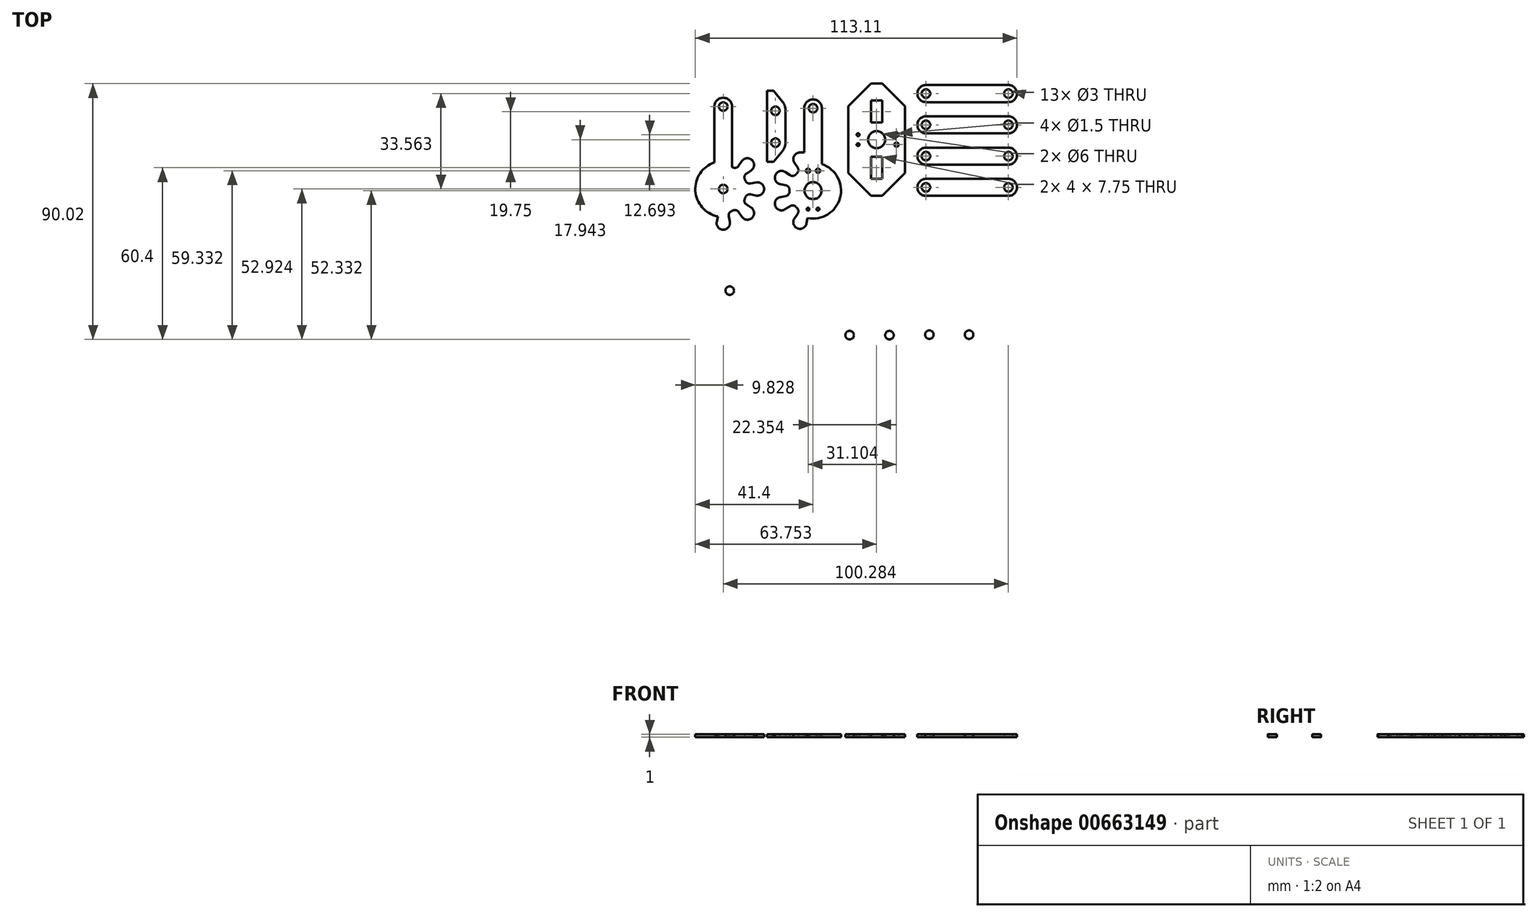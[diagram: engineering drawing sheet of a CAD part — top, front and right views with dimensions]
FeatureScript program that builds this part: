
annotation { "Feature Type Name" : "Feature", "Feature Type Description" : "" }
export const myFeature = defineFeature(function(context is Context, id is Id, definition is map)
    precondition{}
    {
        {
            var Q0;
            Q0=qCreatedBy(makeId("Top.planeOp"),FACE);
            var sketch = newSketch(context, id + "F0", { "sketchPlane" : qUnion([Q0])});
            skCircle(sketch, "E0", {"center": v(-44.1, -27.1) * mm, "radius": 1.5 * mm});
            skLineSegment(sketch, "E1", {"start": v(-8.4, -41.1) * mm, "end": v(-8.4, -22.47) * mm});
            skLineSegment(sketch, "E2", {"start": v(-26.87, -6.6) * mm, "end": v(-38.44, -6.6) * mm});
            skLineSegment(sketch, "E3", {"start": v(-56.9, -22.47) * mm, "end": v(-56.9, -41.1) * mm});
            skCircle(sketch, "E4", {"center": v(-38.1, -10.13) * mm, "radius": 1.5 * mm});
            skCircle(sketch, "E5", {"center": v(-26.9, -10.13) * mm, "radius": 1.5 * mm});
            skLineSegment(sketch, "E6", {"start": v(-14.3, -20.65) * mm, "end": v(-37, -20.65) * mm, "construction": true});
            skLineSegment(sketch, "E7", {"start": v(-37, -33.55) * mm, "end": v(-14.3, -33.55) * mm, "construction": true});
            skLineSegment(sketch, "E8", {"start": v(-14.3, -20.65) * mm, "end": v(-14.3, -33.55) * mm, "construction": true});
            skLineSegment(sketch, "E9", {"start": v(-37, -20.65) * mm, "end": v(-37, -33.55) * mm, "construction": true});
            skLineSegment(sketch, "E10", {"start": v(-9.72, -19.29) * mm, "end": v(-24.02, -7.62) * mm});
            skLineSegment(sketch, "E11", {"start": v(-41.28, -7.62) * mm, "end": v(-55.58, -19.29) * mm});
            skArc(sketch, "E12", {"start": v(-8.4, -22.47) * mm, "mid": v(-8.74, -20.75) * mm, "end": v(-9.72, -19.29) * mm});
            skArc(sketch, "E13", {"start": v(-55.58, -19.29) * mm, "mid": v(-56.56, -20.75) * mm, "end": v(-56.9, -22.47) * mm});
            skArc(sketch, "E14", {"start": v(-12.9, -45.6) * mm, "mid": v(-9.72, -44.29) * mm, "end": v(-8.4, -41.1) * mm});
            skArc(sketch, "E15", {"start": v(-56.9, -41.1) * mm, "mid": v(-55.58, -44.29) * mm, "end": v(-52.4, -45.6) * mm});
            skLineSegment(sketch, "E16", {"start": v(-52.4, -45.6) * mm, "end": v(-52.4, -41.6) * mm});
            skLineSegment(sketch, "E17", {"start": v(-52.4, -41.6) * mm, "end": v(-46.4, -41.6) * mm});
            skLineSegment(sketch, "E18", {"start": v(-46.4, -41.6) * mm, "end": v(-46.4, -45.6) * mm});
            skLineSegment(sketch, "E19", {"start": v(-12.9, -45.6) * mm, "end": v(-12.9, -41.6) * mm});
            skLineSegment(sketch, "E20", {"start": v(-12.9, -41.6) * mm, "end": v(-18.9, -41.6) * mm});
            skLineSegment(sketch, "E21", {"start": v(-18.9, -41.6) * mm, "end": v(-18.9, -45.6) * mm});
            skLineSegment(sketch, "E22", {"start": v(-38.65, -41.6) * mm, "end": v(-26.65, -41.6) * mm});
            skLineSegment(sketch, "E23", {"start": v(-26.65, -41.6) * mm, "end": v(-26.65, -45.6) * mm});
            skLineSegment(sketch, "E24", {"start": v(-38.65, -41.6) * mm, "end": v(-38.65, -45.6) * mm});
            skArc(sketch, "E25", {"start": v(-24.02, -7.62) * mm, "mid": v(-25.36, -6.86) * mm, "end": v(-26.87, -6.6) * mm});
            skArc(sketch, "E26", {"start": v(-38.44, -6.6) * mm, "mid": v(-39.95, -6.86) * mm, "end": v(-41.28, -7.62) * mm});
            skLineSegment(sketch, "E27", {"start": v(-46.4, -45.6) * mm, "end": v(-38.65, -45.6) * mm});
            skLineSegment(sketch, "E28", {"start": v(-26.65, -45.6) * mm, "end": v(-18.9, -45.6) * mm});
            skCircle(sketch, "E29", {"center": v(-39.9, -27.1) * mm, "radius": 0.9 * mm});
            skCircle(sketch, "E30", {"center": v(-11.4, -27.1) * mm, "radius": 0.9 * mm});
            skCircle(sketch, "E31", {"center": v(-11, -8.76) * mm, "radius": 3 * mm});
            skCircle(sketch, "E32", {"center": v(-11, -8.76) * mm, "radius": 1.5 * mm});
            skCircle(sketch, "E33", {"center": v(12.07, -42.76) * mm, "radius": 1.5 * mm});
            skCircle(sketch, "E34", {"center": v(18.07, -25.8) * mm, "radius": 1.5 * mm});
            skLineSegment(sketch, "E35", {"start": v(23.57, -22.8) * mm, "end": v(23.57, 2.2) * mm});
            skLineSegment(sketch, "E36", {"start": v(23.57, 2.2) * mm, "end": v(17.07, 2.2) * mm});
            skLineSegment(sketch, "E37", {"start": v(17.07, 2.2) * mm, "end": v(17.07, -22.8) * mm});
            skLineSegment(sketch, "E38", {"start": v(17.07, -22.8) * mm, "end": v(15.57, -22.8) * mm});
            skLineSegment(sketch, "E39", {"start": v(9.2, -41.89) * mm, "end": v(15.57, -22.8) * mm});
            skLineSegment(sketch, "E40", {"start": v(14.87, -43.83) * mm, "end": v(23.57, -22.8) * mm});
            skArc(sketch, "E41", {"start": v(9.2, -41.89) * mm, "mid": v(11.1, -45.6) * mm, "end": v(14.87, -43.83) * mm});
            skLineSegment(sketch, "E42", {"start": v(24.9, 45.23) * mm, "end": v(53.9, 45.23) * mm});
            skLineSegment(sketch, "E43", {"start": v(53.9, 39.23) * mm, "end": v(24.9, 39.23) * mm});
            skArc(sketch, "E44", {"start": v(24.9, 45.23) * mm, "mid": v(21.9, 42.23) * mm, "end": v(24.9, 39.23) * mm});
            skArc(sketch, "E45", {"start": v(53.9, 39.23) * mm, "mid": v(56.9, 42.23) * mm, "end": v(53.9, 45.23) * mm});
            skCircle(sketch, "E46", {"center": v(24.9, 42.23) * mm, "radius": 1.5 * mm});
            skCircle(sketch, "E47", {"center": v(53.9, 42.23) * mm, "radius": 1.5 * mm});
            skLineSegment(sketch, "E48", {"start": v(17.54, 37.76) * mm, "end": v(17.54, 14.26) * mm});
            skLineSegment(sketch, "E49", {"start": v(9.54, 6.26) * mm, "end": v(17.54, 14.26) * mm});
            skLineSegment(sketch, "E50", {"start": v(9.54, 6.26) * mm, "end": v(5.54, 6.26) * mm});
            skLineSegment(sketch, "E51", {"start": v(-2.46, 14.26) * mm, "end": v(5.54, 6.26) * mm});
            skLineSegment(sketch, "E52", {"start": v(-2.46, 14.26) * mm, "end": v(-2.46, 37.76) * mm});
            skLineSegment(sketch, "E53", {"start": v(5.54, 45.76) * mm, "end": v(9.54, 45.76) * mm});
            skLineSegment(sketch, "E54", {"start": v(-2.46, 37.76) * mm, "end": v(5.54, 45.76) * mm});
            skLineSegment(sketch, "E55", {"start": v(17.54, 37.76) * mm, "end": v(9.54, 45.76) * mm});
            skLineSegment(sketch, "E56", {"start": v(5.54, 39.76) * mm, "end": v(9.54, 39.76) * mm});
            skLineSegment(sketch, "E57", {"start": v(9.54, 39.76) * mm, "end": v(9.54, 32.01) * mm});
            skLineSegment(sketch, "E58", {"start": v(9.54, 32.01) * mm, "end": v(5.54, 32.01) * mm});
            skLineSegment(sketch, "E59", {"start": v(5.54, 32.01) * mm, "end": v(5.54, 39.76) * mm});
            skLineSegment(sketch, "E60", {"start": v(5.54, 20.01) * mm, "end": v(9.54, 20.01) * mm});
            skLineSegment(sketch, "E61", {"start": v(9.54, 20.01) * mm, "end": v(9.54, 12.26) * mm});
            skLineSegment(sketch, "E62", {"start": v(9.54, 12.26) * mm, "end": v(5.54, 12.26) * mm});
            skLineSegment(sketch, "E63", {"start": v(5.54, 12.26) * mm, "end": v(5.54, 20.01) * mm});
            skCircle(sketch, "E64", {"center": v(7.54, 26.01) * mm, "radius": 3 * mm});
            skCircle(sketch, "E65", {"center": v(14.54, 27.76) * mm, "radius": 0.75 * mm});
            skCircle(sketch, "E66", {"center": v(14.54, 24.26) * mm, "radius": 0.75 * mm});
            skCircle(sketch, "E67", {"center": v(1.04, 27.76) * mm, "radius": 0.5 * mm});
            skCircle(sketch, "E68", {"center": v(1.04, 24.26) * mm, "radius": 0.5 * mm});
            skLineSegment(sketch, "E69", {"start": v(-40.97, 0.55) * mm, "end": v(-39.86, -1.12) * mm});
            skArc(sketch, "E70", {"start": v(-40.97, 0.55) * mm, "mid": v(-41.85, 1.19) * mm, "end": v(-42.93, 1.1) * mm});
            skArc(sketch, "E71", {"start": v(-43.48, 0.88) * mm, "mid": v(-43.2, 0.99) * mm, "end": v(-42.93, 1.1) * mm});
            skArc(sketch, "E72", {"start": v(-43.48, 0.88) * mm, "mid": v(-44.3, 0.17) * mm, "end": v(-44.47, -0.9) * mm});
            skLineSegment(sketch, "E73", {"start": v(-44.07, -2.86) * mm, "end": v(-44.47, -0.9) * mm});
            skArc(sketch, "E74", {"start": v(-44.04, -3.08) * mm, "mid": v(-44.05, -2.97) * mm, "end": v(-44.07, -2.86) * mm});
            skArc(sketch, "E75", {"start": v(-48.69, -2.86) * mm, "mid": v(-48.7, -2.97) * mm, "end": v(-48.72, -3.08) * mm});
            skLineSegment(sketch, "E76", {"start": v(-48.31, -0.98) * mm, "end": v(-48.69, -2.86) * mm});
            skArc(sketch, "E77", {"start": v(-42.93, 16.22) * mm, "mid": v(-43.1, 16.3) * mm, "end": v(-43.28, 16.37) * mm});
            skArc(sketch, "E78", {"start": v(-42.93, 16.22) * mm, "mid": v(-41.85, 16.14) * mm, "end": v(-40.97, 16.78) * mm});
            skLineSegment(sketch, "E79", {"start": v(-39.86, 18.45) * mm, "end": v(-40.97, 16.78) * mm});
            skArc(sketch, "E80", {"start": v(-39.73, 18.62) * mm, "mid": v(-39.8, 18.54) * mm, "end": v(-39.86, 18.45) * mm});
            skArc(sketch, "E81", {"start": v(-36.6, 15.18) * mm, "mid": v(-36.5, 15.25) * mm, "end": v(-36.42, 15.31) * mm});
            skLineSegment(sketch, "E82", {"start": v(-38.26, 14.07) * mm, "end": v(-36.6, 15.18) * mm});
            skArc(sketch, "E83", {"start": v(-38.26, 14.07) * mm, "mid": v(-38.9, 13.2) * mm, "end": v(-38.82, 12.12) * mm});
            skArc(sketch, "E84", {"start": v(-38.6, 11.57) * mm, "mid": v(-38.7, 11.84) * mm, "end": v(-38.82, 12.12) * mm});
            skArc(sketch, "E85", {"start": v(-38.6, 11.57) * mm, "mid": v(-37.89, 10.75) * mm, "end": v(-36.82, 10.58) * mm});
            skLineSegment(sketch, "E86", {"start": v(-34.6, 11) * mm, "end": v(-36.82, 10.58) * mm});
            skLineSegment(sketch, "E87", {"start": v(-36.82, 6.75) * mm, "end": v(-34.6, 6.32) * mm});
            skArc(sketch, "E88", {"start": v(-36.82, 6.75) * mm, "mid": v(-37.89, 6.58) * mm, "end": v(-38.6, 5.76) * mm});
            skArc(sketch, "E89", {"start": v(-38.82, 5.21) * mm, "mid": v(-38.7, 5.48) * mm, "end": v(-38.6, 5.76) * mm});
            skArc(sketch, "E90", {"start": v(-38.82, 5.21) * mm, "mid": v(-38.9, 4.13) * mm, "end": v(-38.26, 3.26) * mm});
            skLineSegment(sketch, "E91", {"start": v(-36.6, 2.15) * mm, "end": v(-38.26, 3.26) * mm});
            skArc(sketch, "E92", {"start": v(-36.42, 2.02) * mm, "mid": v(-36.5, 2.08) * mm, "end": v(-36.6, 2.15) * mm});
            skArc(sketch, "E93", {"start": v(-39.86, -1.12) * mm, "mid": v(-39.8, -1.2) * mm, "end": v(-39.73, -1.3) * mm});
            skArc(sketch, "E94", {"start": v(-48.73, -3.1) * mm, "mid": v(-46.38, -5.68) * mm, "end": v(-44.04, -3.1) * mm});
            skArc(sketch, "E95", {"start": v(-34.6, 6.32) * mm, "mid": v(-32.04, 8.66) * mm, "end": v(-34.6, 11) * mm});
            skArc(sketch, "E96", {"start": v(-36.4, 15.33) * mm, "mid": v(-36.24, 18.8) * mm, "end": v(-39.71, 18.65) * mm});
            skArc(sketch, "E97", {"start": v(-39.71, -1.32) * mm, "mid": v(-36.24, -1.48) * mm, "end": v(-36.4, 2) * mm});
            skArc(sketch, "E98", {"start": v(-36.42, 15.31) * mm, "mid": v(-36.41, 15.32) * mm, "end": v(-36.4, 15.33) * mm});
            skArc(sketch, "E99", {"start": v(-39.71, 18.65) * mm, "mid": v(-39.72, 18.63) * mm, "end": v(-39.73, 18.62) * mm});
            skArc(sketch, "E100", {"start": v(-48.72, -3.08) * mm, "mid": v(-48.72, -3.1) * mm, "end": v(-48.73, -3.1) * mm});
            skArc(sketch, "E101", {"start": v(-44.04, -3.1) * mm, "mid": v(-44.04, -3.1) * mm, "end": v(-44.04, -3.08) * mm});
            skArc(sketch, "E102", {"start": v(-39.73, -1.3) * mm, "mid": v(-39.72, -1.3) * mm, "end": v(-39.71, -1.32) * mm});
            skArc(sketch, "E103", {"start": v(-36.4, 2) * mm, "mid": v(-36.41, 2) * mm, "end": v(-36.42, 2.02) * mm});
            skLineSegment(sketch, "E104", {"start": v(-43.28, 37.66) * mm, "end": v(-43.28, 16.37) * mm});
            skLineSegment(sketch, "E105", {"start": v(-49.49, 37.66) * mm, "end": v(-49.49, 18) * mm});
            skArc(sketch, "E106", {"start": v(-49.49, 18) * mm, "mid": v(-56.2, 8.06) * mm, "end": v(-48.31, -0.98) * mm});
            skCircle(sketch, "E107", {"center": v(-46.38, 8.66) * mm, "radius": 1.5 * mm});
            skCircle(sketch, "E108", {"center": v(-46.38, 37.66) * mm, "radius": 1.5 * mm});
            skArc(sketch, "E109", {"start": v(-43.28, 37.66) * mm, "mid": v(-46.38, 40.77) * mm, "end": v(-49.49, 37.66) * mm});
            skLineSegment(sketch, "E110", {"start": v(-24.51, 24.93) * mm, "end": v(-24.51, 36.5) * mm});
            skCircle(sketch, "E111", {"center": v(-28.04, 36.16) * mm, "radius": 1.5 * mm});
            skCircle(sketch, "E112", {"center": v(-28.04, 24.96) * mm, "radius": 1.5 * mm});
            skLineSegment(sketch, "E113", {"start": v(-28.69, 18.2) * mm, "end": v(-25.53, 22.08) * mm});
            skLineSegment(sketch, "E114", {"start": v(-25.53, 39.34) * mm, "end": v(-28.69, 43.2) * mm});
            skArc(sketch, "E115", {"start": v(-25.53, 22.08) * mm, "mid": v(-24.77, 23.42) * mm, "end": v(-24.51, 24.93) * mm});
            skArc(sketch, "E116", {"start": v(-24.51, 36.5) * mm, "mid": v(-24.77, 38) * mm, "end": v(-25.53, 39.34) * mm});
            skLineSegment(sketch, "E117", {"start": v(-31.01, 43.2) * mm, "end": v(-31.01, 18.2) * mm});
            skLineSegment(sketch, "E118", {"start": v(-31.01, 18.2) * mm, "end": v(-28.69, 18.2) * mm});
            skLineSegment(sketch, "E119", {"start": v(-31.01, 43.2) * mm, "end": v(-28.69, 43.2) * mm});
            skLineSegment(sketch, "E120", {"start": v(-11.7, 37.07) * mm, "end": v(-11.7, 17.4) * mm});
            skLineSegment(sketch, "E121", {"start": v(-17.92, 37.07) * mm, "end": v(-17.92, 21.5) * mm});
            skLineSegment(sketch, "E122", {"start": v(-17.09, -3.46) * mm, "end": v(-16.72, -1.57) * mm});
            skArc(sketch, "E123", {"start": v(-17.14, -3.67) * mm, "mid": v(-17.11, -3.57) * mm, "end": v(-17.09, -3.46) * mm});
            skArc(sketch, "E124", {"start": v(-21.35, -1.7) * mm, "mid": v(-21.41, -1.79) * mm, "end": v(-21.47, -1.88) * mm});
            skLineSegment(sketch, "E125", {"start": v(-20.24, -0.03) * mm, "end": v(-21.35, -1.7) * mm});
            skArc(sketch, "E126", {"start": v(-20.24, -0.03) * mm, "mid": v(-19.98, 1.02) * mm, "end": v(-20.47, 2) * mm});
            skArc(sketch, "E127", {"start": v(-20.9, 2.4) * mm, "mid": v(-20.69, 2.2) * mm, "end": v(-20.47, 2) * mm});
            skArc(sketch, "E128", {"start": v(-20.9, 2.4) * mm, "mid": v(-21.86, 2.9) * mm, "end": v(-22.91, 2.64) * mm});
            skLineSegment(sketch, "E129", {"start": v(-24.58, 1.53) * mm, "end": v(-22.91, 2.64) * mm});
            skArc(sketch, "E130", {"start": v(-24.76, 1.42) * mm, "mid": v(-24.67, 1.47) * mm, "end": v(-24.58, 1.53) * mm});
            skArc(sketch, "E131", {"start": v(-26.34, 5.8) * mm, "mid": v(-26.45, 5.77) * mm, "end": v(-26.55, 5.74) * mm});
            skLineSegment(sketch, "E132", {"start": v(-24.38, 6.18) * mm, "end": v(-26.34, 5.8) * mm});
            skArc(sketch, "E133", {"start": v(-24.38, 6.18) * mm, "mid": v(-23.45, 6.75) * mm, "end": v(-23.12, 7.78) * mm});
            skArc(sketch, "E134", {"start": v(-23.12, 8.37) * mm, "mid": v(-23.12, 8.07) * mm, "end": v(-23.12, 7.78) * mm});
            skArc(sketch, "E135", {"start": v(-23.12, 8.37) * mm, "mid": v(-23.45, 9.4) * mm, "end": v(-24.38, 9.96) * mm});
            skLineSegment(sketch, "E136", {"start": v(-26.34, 10.35) * mm, "end": v(-24.38, 9.96) * mm});
            skArc(sketch, "E137", {"start": v(-26.55, 10.4) * mm, "mid": v(-26.45, 10.37) * mm, "end": v(-26.34, 10.35) * mm});
            skArc(sketch, "E138", {"start": v(-24.58, 14.62) * mm, "mid": v(-24.67, 14.67) * mm, "end": v(-24.76, 14.73) * mm});
            skLineSegment(sketch, "E139", {"start": v(-22.91, 13.5) * mm, "end": v(-24.58, 14.62) * mm});
            skArc(sketch, "E140", {"start": v(-22.91, 13.5) * mm, "mid": v(-21.86, 13.25) * mm, "end": v(-20.9, 13.74) * mm});
            skArc(sketch, "E141", {"start": v(-20.47, 14.15) * mm, "mid": v(-20.69, 13.95) * mm, "end": v(-20.9, 13.74) * mm});
            skArc(sketch, "E142", {"start": v(-20.47, 14.15) * mm, "mid": v(-19.98, 15.12) * mm, "end": v(-20.24, 16.18) * mm});
            skLineSegment(sketch, "E143", {"start": v(-21.35, 17.84) * mm, "end": v(-20.24, 16.18) * mm});
            skArc(sketch, "E144", {"start": v(-21.47, 18.02) * mm, "mid": v(-21.41, 17.93) * mm, "end": v(-21.35, 17.84) * mm});
            skArc(sketch, "E145", {"start": v(-21.48, -1.9) * mm, "mid": v(-20.3, -5.18) * mm, "end": v(-17.15, -3.7) * mm});
            skArc(sketch, "E146", {"start": v(-24.79, 14.74) * mm, "mid": v(-28.06, 13.56) * mm, "end": v(-26.58, 10.41) * mm});
            skArc(sketch, "E147", {"start": v(-26.58, 5.73) * mm, "mid": v(-28.06, 2.58) * mm, "end": v(-24.79, 1.4) * mm});
            skArc(sketch, "E148", {"start": v(-19.4, 21.5) * mm, "mid": v(-21.41, 20.36) * mm, "end": v(-21.48, 18.05) * mm});
            skArc(sketch, "E149", {"start": v(-26.55, 5.74) * mm, "mid": v(-26.57, 5.74) * mm, "end": v(-26.58, 5.73) * mm});
            skArc(sketch, "E150", {"start": v(-24.79, 1.4) * mm, "mid": v(-24.78, 1.4) * mm, "end": v(-24.76, 1.42) * mm});
            skArc(sketch, "E151", {"start": v(-21.47, -1.88) * mm, "mid": v(-21.47, -1.9) * mm, "end": v(-21.48, -1.9) * mm});
            skArc(sketch, "E152", {"start": v(-17.15, -3.7) * mm, "mid": v(-17.15, -3.69) * mm, "end": v(-17.14, -3.67) * mm});
            skArc(sketch, "E153", {"start": v(-21.48, 18.05) * mm, "mid": v(-21.47, 18.04) * mm, "end": v(-21.47, 18.02) * mm});
            skArc(sketch, "E154", {"start": v(-24.76, 14.73) * mm, "mid": v(-24.78, 14.74) * mm, "end": v(-24.79, 14.74) * mm});
            skArc(sketch, "E155", {"start": v(-26.58, 10.41) * mm, "mid": v(-26.57, 10.4) * mm, "end": v(-26.55, 10.4) * mm});
            skArc(sketch, "E156", {"start": v(-16.72, -1.57) * mm, "mid": v(-5.3, 5.56) * mm, "end": v(-11.7, 17.4) * mm});
            skLineSegment(sketch, "E157", {"start": v(-19.4, 21.5) * mm, "end": v(-17.92, 21.5) * mm});
            skCircle(sketch, "E158", {"center": v(-14.81, 37.07) * mm, "radius": 1.5 * mm});
            skArc(sketch, "E159", {"start": v(-11.7, 37.07) * mm, "mid": v(-14.81, 40.18) * mm, "end": v(-17.92, 37.07) * mm});
            skCircle(sketch, "E160", {"center": v(40.1, -42.6) * mm, "radius": 1.5 * mm});
            skCircle(sketch, "E161", {"center": v(46.1, -25.63) * mm, "radius": 1.5 * mm});
            skLineSegment(sketch, "E162", {"start": v(51.6, -22.63) * mm, "end": v(51.6, 2.37) * mm});
            skLineSegment(sketch, "E163", {"start": v(51.6, 2.37) * mm, "end": v(45.1, 2.37) * mm});
            skLineSegment(sketch, "E164", {"start": v(45.1, 2.37) * mm, "end": v(45.1, -22.63) * mm});
            skLineSegment(sketch, "E165", {"start": v(45.1, -22.63) * mm, "end": v(43.6, -22.63) * mm});
            skLineSegment(sketch, "E166", {"start": v(37.23, -41.73) * mm, "end": v(43.6, -22.63) * mm});
            skLineSegment(sketch, "E167", {"start": v(42.9, -43.66) * mm, "end": v(51.6, -22.63) * mm});
            skArc(sketch, "E168", {"start": v(37.23, -41.73) * mm, "mid": v(39.13, -45.44) * mm, "end": v(42.9, -43.66) * mm});
            skCircle(sketch, "E169", {"center": v(26.1, -42.6) * mm, "radius": 1.5 * mm});
            skCircle(sketch, "E170", {"center": v(32.1, -25.63) * mm, "radius": 1.5 * mm});
            skLineSegment(sketch, "E171", {"start": v(37.6, -22.63) * mm, "end": v(37.6, 2.37) * mm});
            skLineSegment(sketch, "E172", {"start": v(37.6, 2.37) * mm, "end": v(31.1, 2.37) * mm});
            skLineSegment(sketch, "E173", {"start": v(31.1, 2.37) * mm, "end": v(31.1, -22.63) * mm});
            skLineSegment(sketch, "E174", {"start": v(31.1, -22.63) * mm, "end": v(29.6, -22.63) * mm});
            skLineSegment(sketch, "E175", {"start": v(23.23, -41.73) * mm, "end": v(29.6, -22.63) * mm});
            skLineSegment(sketch, "E176", {"start": v(28.9, -43.66) * mm, "end": v(37.6, -22.63) * mm});
            skArc(sketch, "E177", {"start": v(23.23, -41.73) * mm, "mid": v(25.13, -45.44) * mm, "end": v(28.9, -43.66) * mm});
            skCircle(sketch, "E178", {"center": v(-1.93, -42.76) * mm, "radius": 1.5 * mm});
            skCircle(sketch, "E179", {"center": v(4.07, -25.8) * mm, "radius": 1.5 * mm});
            skLineSegment(sketch, "E180", {"start": v(9.57, -22.8) * mm, "end": v(9.57, 2.2) * mm});
            skLineSegment(sketch, "E181", {"start": v(9.57, 2.2) * mm, "end": v(3.07, 2.2) * mm});
            skLineSegment(sketch, "E182", {"start": v(3.07, 2.2) * mm, "end": v(3.07, -22.8) * mm});
            skLineSegment(sketch, "E183", {"start": v(3.07, -22.8) * mm, "end": v(1.57, -22.8) * mm});
            skLineSegment(sketch, "E184", {"start": v(-4.8, -41.89) * mm, "end": v(1.57, -22.8) * mm});
            skLineSegment(sketch, "E185", {"start": v(0.87, -43.83) * mm, "end": v(9.57, -22.8) * mm});
            skArc(sketch, "E186", {"start": v(-4.8, -41.89) * mm, "mid": v(-2.9, -45.6) * mm, "end": v(0.87, -43.83) * mm});
            skLineSegment(sketch, "E187", {"start": v(24.9, 34.23) * mm, "end": v(53.9, 34.23) * mm});
            skLineSegment(sketch, "E188", {"start": v(53.9, 28.23) * mm, "end": v(24.9, 28.23) * mm});
            skArc(sketch, "E189", {"start": v(24.9, 34.23) * mm, "mid": v(21.9, 31.23) * mm, "end": v(24.9, 28.23) * mm});
            skArc(sketch, "E190", {"start": v(53.9, 28.23) * mm, "mid": v(56.9, 31.23) * mm, "end": v(53.9, 34.23) * mm});
            skCircle(sketch, "E191", {"center": v(24.9, 31.23) * mm, "radius": 1.5 * mm});
            skCircle(sketch, "E192", {"center": v(53.9, 31.23) * mm, "radius": 1.5 * mm});
            skLineSegment(sketch, "E193", {"start": v(24.9, 12.23) * mm, "end": v(53.9, 12.23) * mm});
            skLineSegment(sketch, "E194", {"start": v(53.9, 6.23) * mm, "end": v(24.9, 6.23) * mm});
            skArc(sketch, "E195", {"start": v(24.9, 12.23) * mm, "mid": v(21.9, 9.23) * mm, "end": v(24.9, 6.23) * mm});
            skArc(sketch, "E196", {"start": v(53.9, 6.23) * mm, "mid": v(56.9, 9.23) * mm, "end": v(53.9, 12.23) * mm});
            skCircle(sketch, "E197", {"center": v(24.9, 9.23) * mm, "radius": 1.5 * mm});
            skCircle(sketch, "E198", {"center": v(53.9, 9.23) * mm, "radius": 1.5 * mm});
            skLineSegment(sketch, "E199", {"start": v(24.9, 23.23) * mm, "end": v(53.9, 23.23) * mm});
            skLineSegment(sketch, "E200", {"start": v(53.9, 17.23) * mm, "end": v(24.9, 17.23) * mm});
            skArc(sketch, "E201", {"start": v(24.9, 23.23) * mm, "mid": v(21.9, 20.23) * mm, "end": v(24.9, 17.23) * mm});
            skArc(sketch, "E202", {"start": v(53.9, 17.23) * mm, "mid": v(56.9, 20.23) * mm, "end": v(53.9, 23.23) * mm});
            skCircle(sketch, "E203", {"center": v(24.9, 20.23) * mm, "radius": 1.5 * mm});
            skCircle(sketch, "E204", {"center": v(53.9, 20.23) * mm, "radius": 1.5 * mm});
            skCircle(sketch, "E205", {"center": v(-14.81, 8.07) * mm, "radius": 3 * mm});
            skCircle(sketch, "E206", {"center": v(-16.56, 15.07) * mm, "radius": 0.75 * mm});
            skCircle(sketch, "E207", {"center": v(-13.06, 15.07) * mm, "radius": 0.75 * mm});
            skCircle(sketch, "E208", {"center": v(-16.56, 1.57) * mm, "radius": 0.5 * mm});
            skCircle(sketch, "E209", {"center": v(-13.06, 1.57) * mm, "radius": 0.5 * mm});
            skLineSegment(sketch, "E210", {"start": v(-32.65, -6.6) * mm, "end": v(-32.65, -41.6) * mm, "construction": true});
            skLineSegment(sketch, "E211", {"start": v(-44.1, -27.1) * mm, "end": v(-32.65, -27.1) * mm, "construction": true});
            skLineSegment(sketch, "E212", {"start": v(-32.65, -27.1) * mm, "end": v(-21.2, -27.1) * mm, "construction": true});
            skCircle(sketch, "E213", {"center": v(-21.2, -27.1) * mm, "radius": 1.5 * mm});
            skSolve(sketch);
        }
        {
            var Q0;
            Q0=makeQuery(id+"F0.imprint","IMPRINT",FACE,{"disambiguationData":[TD([[makeQuery(id+"F0.imprint","IMPRINT",EDGE,{"derivedFrom":sQuery(id+"F0.wireOp",EDGE,"E120")}),-1.0]])]});
            var Q1;
            Q1=makeQuery(id+"F0.imprint","IMPRINT",FACE,{"disambiguationData":[TD([[makeQuery(id+"F0.imprint","IMPRINT",EDGE,{"derivedFrom":sQuery(id+"F0.wireOp",EDGE,"E110")}),1.0]])]});
            var Q2;
            Q2=makeQuery(id+"F0.imprint","IMPRINT",FACE,{"disambiguationData":[TD([[makeQuery(id+"F0.imprint","IMPRINT",EDGE,{"derivedFrom":sQuery(id+"F0.wireOp",EDGE,"E69")}),1.0]])]});
            var Q3;
            Q3=makeQuery(id+"F0.imprint","IMPRINT",FACE,{"disambiguationData":[TD([[makeQuery(id+"F0.imprint","IMPRINT",EDGE,{"derivedFrom":sQuery(id+"F0.wireOp",EDGE,"E48")}),-1.0]])]});
            var Q4;
            Q4=makeQuery(id+"F0.imprint","IMPRINT",FACE,{"disambiguationData":[TD([[makeQuery(id+"F0.imprint","IMPRINT",EDGE,{"derivedFrom":sQuery(id+"F0.wireOp",EDGE,"E42")}),-1.0]])]});
            var Q5;
            Q5=makeQuery(id+"F0.imprint","IMPRINT",FACE,{"disambiguationData":[TD([[makeQuery(id+"F0.imprint","IMPRINT",EDGE,{"derivedFrom":sQuery(id+"F0.wireOp",EDGE,"E187")}),-1.0]])]});
            var Q6;
            Q6=makeQuery(id+"F0.imprint","IMPRINT",FACE,{"disambiguationData":[TD([[makeQuery(id+"F0.imprint","IMPRINT",EDGE,{"derivedFrom":sQuery(id+"F0.wireOp",EDGE,"E199")}),-1.0]])]});
            var Q7;
            Q7=makeQuery(id+"F0.imprint","IMPRINT",FACE,{"disambiguationData":[TD([[makeQuery(id+"F0.imprint","IMPRINT",EDGE,{"derivedFrom":sQuery(id+"F0.wireOp",EDGE,"E193")}),-1.0]])]});
            var Q8;
            Q8=makeQuery(id+"F0.imprint","IMPRINT",FACE,{"disambiguationData":[TD([[makeQuery(id+"F0.imprint","IMPRINT",EDGE,{"derivedFrom":sQuery(id+"F0.wireOp",EDGE,"E178")}),1.0]])]});
            var Q9;
            Q9=makeQuery(id+"F0.imprint","IMPRINT",FACE,{"disambiguationData":[TD([[makeQuery(id+"F0.imprint","IMPRINT",EDGE,{"derivedFrom":sQuery(id+"F0.wireOp",EDGE,"E33")}),1.0]])]});
            var Q10;
            Q10=makeQuery(id+"F0.imprint","IMPRINT",FACE,{"disambiguationData":[TD([[makeQuery(id+"F0.imprint","IMPRINT",EDGE,{"derivedFrom":sQuery(id+"F0.wireOp",EDGE,"E169")}),1.0]])]});
            var Q11;
            Q11=makeQuery(id+"F0.imprint","IMPRINT",FACE,{"disambiguationData":[TD([[makeQuery(id+"F0.imprint","IMPRINT",EDGE,{"derivedFrom":sQuery(id+"F0.wireOp",EDGE,"E160")}),1.0]])]});
            var Q12;
            Q12=makeQuery(id+"F0.imprint","IMPRINT",FACE,{"disambiguationData":[TD([[makeQuery(id+"F0.imprint","IMPRINT",EDGE,{"derivedFrom":sQuery(id+"F0.wireOp",EDGE,"E0")}),1.0]])]});
            extrude(context, id + "F1", {"entities" : qUnion([Q0, Q1, Q2, Q3, Q4, Q5, Q6, Q7, Q8, Q9, Q10, Q11, Q12]), "depth" : 1 * mm, "offsetDistance" : 25 * mm});
        }
    });
